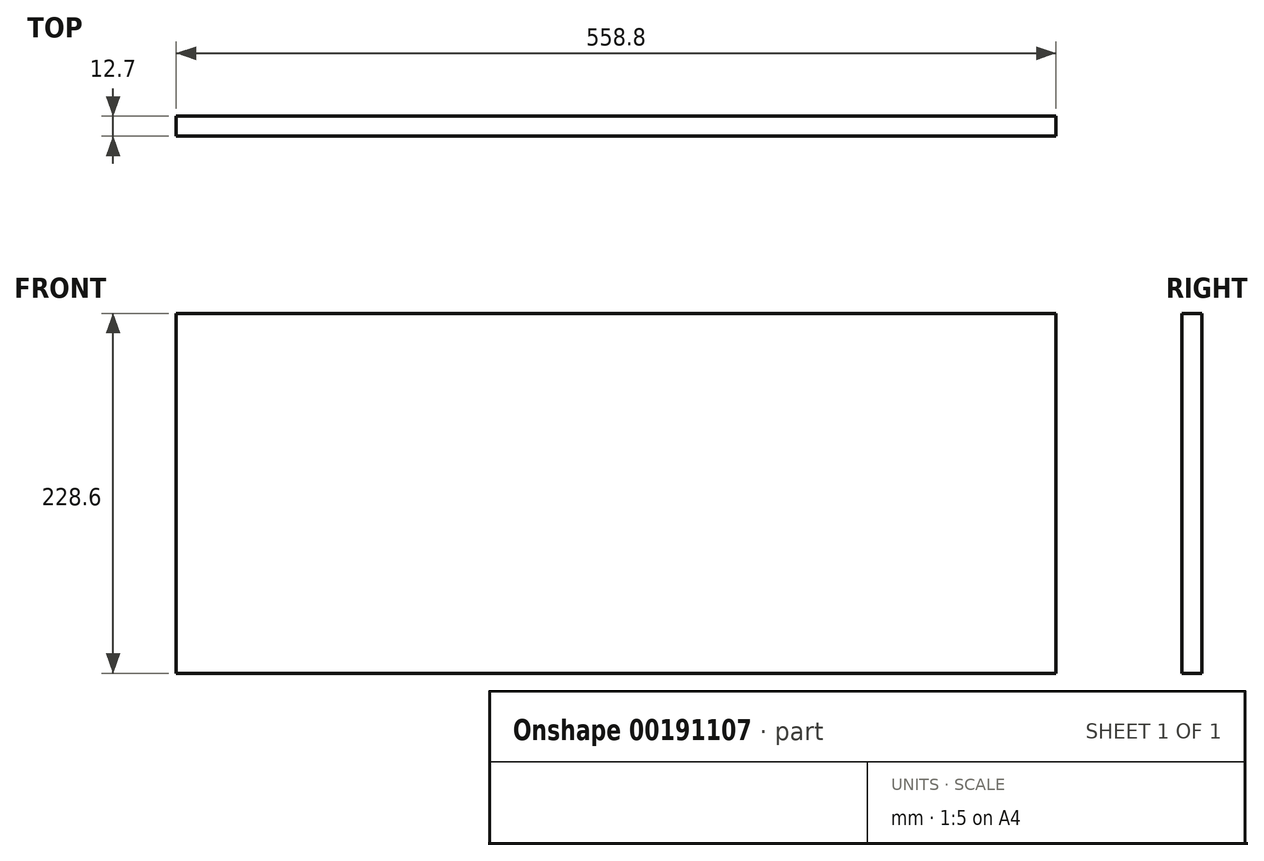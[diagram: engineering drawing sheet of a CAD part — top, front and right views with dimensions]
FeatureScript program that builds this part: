
annotation { "Feature Type Name" : "Feature", "Feature Type Description" : "" }
export const myFeature = defineFeature(function(context is Context, id is Id, definition is map)
    precondition{}
    {
        {
            var Q0;
            Q0=qCreatedBy(makeId("Front.planeOp"),FACE);
            var sketch = newSketch(context, id + "F0", { "sketchPlane" : qUnion([Q0])});
            skLineSegment(sketch, "E0.bottom", {"start": v(279.4, 114.3) * mm, "end": v(-279.4, 114.3) * mm});
            skLineSegment(sketch, "E0.top", {"start": v(279.4, -114.3) * mm, "end": v(-279.4, -114.3) * mm});
            skLineSegment(sketch, "E0.left", {"start": v(279.4, 114.3) * mm, "end": v(279.4, -114.3) * mm});
            skLineSegment(sketch, "E0.right", {"start": v(-279.4, 114.3) * mm, "end": v(-279.4, -114.3) * mm});
            skPoint(sketch, "E0.middle", {"position": v(0, 0) * mm});
            skSolve(sketch);
        }
        {
            var Q0;
            Q0 = qSketchRegion(id + "F0", true);
            extrude(context, id + "F1", {"entities" : qUnion([Q0]), "depth" : 12.7 * mm});
        }
    });
